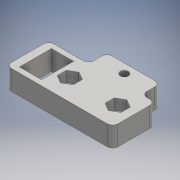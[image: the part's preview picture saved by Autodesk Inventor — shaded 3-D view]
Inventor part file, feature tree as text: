
AUTODESK INVENTOR PART (.ipt)
format: ipt  version: 2016 SP1 (Build 200210100, 210)  size: 180,736 bytes
history: native  units: mm
features: extrude x4, sketch x4, reference x3, fillet x1, projected_geometry x1
ambient origin geometry x8: Origin, YZ Plane, XZ Plane, XY Plane, X Axis, Y Axis, Z Axis, Center Point
bodies: Solid1 (feature_tree)
feature tree (13):
  extrude  "Extrusion1"  Depth=3.0mm
  extrude  "Extrusion2"  Depth=4.0mm
  extrude  "Extrusion3"  Depth=1.0mm
  extrude  "Extrusion4"  Depth=2.0mm
  fillet  "Fillet1"  Radius=7.5mm
  sketch  "Sketch1"  dims[d0=3.0mm d1=3.0mm]
  reference  "Reference1"
  reference  "Reference2"
  sketch  "Sketch2"  dims[d2=3.0mm d3=4.0mm]
  sketch  "Sketch3"  dims[d4=1.0mm d5=1.0mm]
  reference  "Reference3"
  sketch  "Sketch4"  dims[d6=1.0mm d7=1.0mm d8=7.5mm d9=0.0mm d10=6.0mm d11=6.0mm d12=4.0mm d13=0.0mm d14=20.0mm d15=2.8mm d16=1.4mm d17=10.0mm d18=7.0mm d19=0.0mm d20=3.0mm d21=20.0mm d22=7.0mm d23=3.5mm d24=10.0mm d25=7.0mm d26=0.0mm d27=2.0mm]
  projected_geometry  "Projected Loop1"
